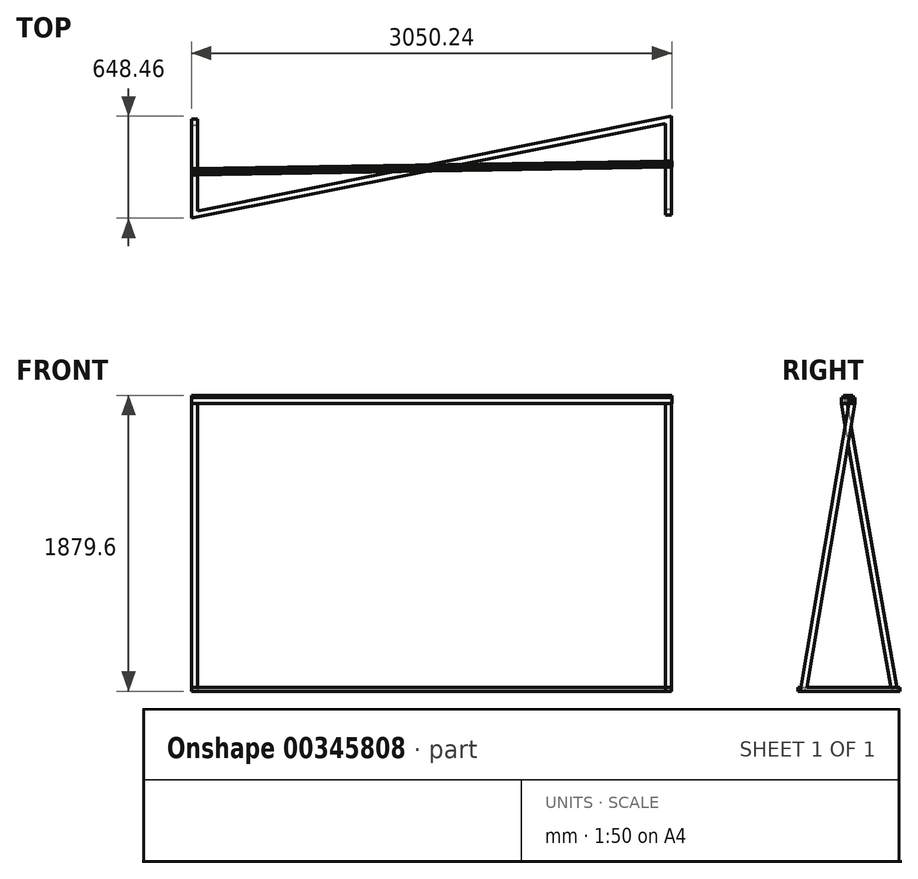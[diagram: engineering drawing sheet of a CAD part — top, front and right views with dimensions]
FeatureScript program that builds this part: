
annotation { "Feature Type Name" : "Feature", "Feature Type Description" : "" }
export const myFeature = defineFeature(function(context is Context, id is Id, definition is map)
    precondition{}
    {
        {
            var Q0;
            Q0=qCreatedBy(makeId("Top.planeOp"),FACE);
            var sketch = newSketch(context, id + "F0", { "sketchPlane" : qUnion([Q0])});
            skLineSegment(sketch, "E0.left", {"start": v(1524, 324.23) * mm, "end": v(1524, -304.8) * mm});
            skLineSegment(sketch, "E0.right", {"start": v(-1524, 304.8) * mm, "end": v(-1524, -324.23) * mm});
            skPoint(sketch, "E0.middle", {"position": v(0, 0) * mm});
            skLineSegment(sketch, "E1", {"start": v(1524, -304.8) * mm, "end": v(1485.9, -304.8) * mm});
            skLineSegment(sketch, "E2", {"start": v(-1485.9, -277.75) * mm, "end": v(-1485.9, 304.8) * mm});
            skLineSegment(sketch, "E3", {"start": v(1485.9, -304.8) * mm, "end": v(1485.9, 277.75) * mm});
            skLineSegment(sketch, "E4", {"start": v(0, 0) * mm, "end": v(-3.74, 18.68) * mm});
            skLineSegment(sketch, "E5", {"start": v(-1485.9, -277.75) * mm, "end": v(1524, 324.23) * mm});
            skLineSegment(sketch, "E6.MirrorCS", {"start": v(-1524, -324.23) * mm, "end": v(1485.9, 277.75) * mm});
            skLineSegment(sketch, "E7", {"start": v(-1524, 304.8) * mm, "end": v(-1485.9, 304.8) * mm});
            skPoint(sketch, "E8", {"position": v(1524, 9.71) * mm});
            skPoint(sketch, "E9", {"position": v(-1524, -9.71) * mm});
            skLineSegment(sketch, "E10.0", {"start": v(1485.78, 24.87) * mm, "end": v(-1386.42, 6.57) * mm});
            skLineSegment(sketch, "E11.MirrorCS", {"start": v(1486.02, -9.58) * mm, "end": v(-1357.54, -27.7) * mm});
            skLineSegment(sketch, "E12", {"start": v(-1357.54, -27.7) * mm, "end": v(-1307.98, -27.39) * mm});
            skLineSegment(sketch, "E13", {"start": v(-1486.02, 5.93) * mm, "end": v(-1485.9, 183.73) * mm});
            skLineSegment(sketch, "E14", {"start": v(-1307.98, -27.39) * mm, "end": v(-1485.9, 183.73) * mm});
            skLineSegment(sketch, "E15", {"start": v(-1307.98, -27.39) * mm, "end": v(-1396.94, 78.17) * mm});
            skLineSegment(sketch, "E16", {"start": v(-1396.94, 78.17) * mm, "end": v(-1426.08, 53.62) * mm});
            skLineSegment(sketch, "E17", {"start": v(-1426.08, 53.62) * mm, "end": v(-1386.42, 6.57) * mm});
            skLineSegment(sketch, "E18", {"start": v(-1357.54, -27.7) * mm, "end": v(-1386.42, 6.57) * mm});
            skLineSegment(sketch, "E19", {"start": v(-1426.08, 53.62) * mm, "end": v(-1485.96, 124.68) * mm});
            skSolve(sketch);
        }
        {
            var Q0;
            {var subQ9=sQuery(id+"F0.wireOp",EDGE,"E0.left");Q0=makeQuery(id+"F0.imprint","IMPRINT",FACE,{"disambiguationData":[TD([[makeQuery(id+"F0.imprint","IMPRINT",EDGE,{"derivedFrom":subQ9}),-1.0]])]});}
            var Q1;
            {var subQ0=sQuery(id+"F0.wireOp",EDGE,"E13");var subQ3=sQuery(id+"F0.wireOp",EDGE,"E19");var subQ5=makeQuery(id+"F0.imprint","INTERSECT",VERTEX,{"derivedFrom":[subQ0,subQ3]});Q1=makeQuery(id+"F0.imprint","IMPRINT",FACE,{"disambiguationData":[TD([[makeQuery(id+"F0.imprint","IMPRINT",EDGE,{"disambiguationData":[TD([[subQ5,1.0]])],"derivedFrom":subQ3}),-1.0]])]});}
            var Q2;
            {var subQ0=sQuery(id+"F0.wireOp",EDGE,"E10.0");var subQ2=sQuery(id+"F0.wireOp",EDGE,"E5");var subQ3=makeQuery(id+"F0.imprint","INTERSECT",VERTEX,{"derivedFrom":[subQ2,subQ0]});Q2=makeQuery(id+"F0.imprint","IMPRINT",FACE,{"disambiguationData":[TD([[makeQuery(id+"F0.imprint","IMPRINT",EDGE,{"disambiguationData":[TD([[subQ3,1.0]])],"derivedFrom":subQ2}),-1.0]])]});}
            var Q3;
            {var subQ0=sQuery(id+"F0.wireOp",EDGE,"E5");var subQ1=sQuery(id+"F0.wireOp",EDGE,"E4");var subQ2=makeQuery(id+"F0.imprint","INTERSECT",VERTEX,{"derivedFrom":[subQ1,subQ0]});Q3=makeQuery(id+"F0.imprint","IMPRINT",FACE,{"disambiguationData":[TD([[makeQuery(id+"F0.imprint","IMPRINT",EDGE,{"disambiguationData":[TD([[subQ2,1.0]])],"derivedFrom":subQ1}),1.0]])]});}
            var Q4;
            {var subQ11=sQuery(id+"F0.wireOp",EDGE,"E0.right");Q4=makeQuery(id+"F0.imprint","IMPRINT",FACE,{"disambiguationData":[TD([[makeQuery(id+"F0.imprint","IMPRINT",EDGE,{"derivedFrom":subQ11}),1.0]])]});}
            extrude(context, id + "F1", {"entities" : qUnion([Q0, Q1, Q2, Q3, Q4]), "depth" : 25.4 * mm});
        }
        {
            var Q0;
            Q0=makeQuery(id+"F1.opExtrude","SWEPT_FACE",FACE,{"disambiguationData":[OSD([sQuery(id+"F0.wireOp",EDGE,"E0.left")])]});
            var sketch = newSketch(context, id + "F2", { "sketchPlane" : qUnion([Q0])});
            skLineSegment(sketch, "E20", {"start": v(0, 0) * mm, "end": v(0, 1828.8) * mm});
            skLineSegment(sketch, "E21", {"start": v(0, 1828.8) * mm, "end": v(-304.8, 25.4) * mm});
            skLineSegment(sketch, "E22", {"start": v(0, 1828.8) * mm, "end": v(37.57, 1822.45) * mm});
            skLineSegment(sketch, "E23", {"start": v(38.64, 1828.8) * mm, "end": v(-266.16, 25.4) * mm});
            skLineSegment(sketch, "E24", {"start": v(38.64, 1828.8) * mm, "end": v(0, 1828.8) * mm});
            skLineSegment(sketch, "E25", {"start": v(-266.16, 25.4) * mm, "end": v(-304.8, 25.4) * mm});
            skSolve(sketch);
        }
        {
            var Q0;
            Q0 = qSketchRegion(id + "F2", true);
            var Q1;
            {var subQ0=sQuery(id+"F2.wireOp",EDGE,"E21");Q1=makeQuery(id+"F2.imprint","IMPRINT",FACE,{"disambiguationData":[TD([[makeQuery(id+"F2.imprint","IMPRINT",EDGE,{"derivedFrom":subQ0}),1.0]])]});}
            extrude(context, id + "F3", {"entities" : qUnion([Q0, Q1]), "operationType" : NewBodyOperationType.ADD, "oppositeDirection" : true, "depth" : 38.1 * mm});
        }
        {
            var Q0;
            Q0=makeQuery(id+"F1.opExtrude","SWEPT_FACE",FACE,{"disambiguationData":[OSD([sQuery(id+"F0.wireOp",EDGE,"E0.right")])]});
            var sketch = newSketch(context, id + "F4", { "sketchPlane" : qUnion([Q0])});
            skLineSegment(sketch, "E26", {"start": v(9.71, 0) * mm, "end": v(9.71, 1828.8) * mm});
            skPoint(sketch, "E26.endSnap0", {"position": v(9.71, 25.4) * mm});
            skLineSegment(sketch, "E27", {"start": v(9.71, 1828.8) * mm, "end": v(-304.8, 25.4) * mm});
            skLineSegment(sketch, "E28", {"start": v(9.71, 1828.8) * mm, "end": v(47.25, 1822.25) * mm});
            skLineSegment(sketch, "E29", {"start": v(48.39, 1828.8) * mm, "end": v(-266.12, 25.4) * mm});
            skLineSegment(sketch, "E30", {"start": v(9.71, 1828.8) * mm, "end": v(49.22, 1828.8) * mm});
            skSolve(sketch);
        }
        {
            var Q0;
            Q0 = qSketchRegion(id + "F4", true);
            var Q1;
            {var subQ0=sQuery(id+"F4.wireOp",EDGE,"E27");Q1=makeQuery(id+"F4.imprint","IMPRINT",FACE,{"disambiguationData":[TD([[makeQuery(id+"F4.imprint","IMPRINT",EDGE,{"derivedFrom":subQ0}),1.0]])]});}
            extrude(context, id + "F5", {"entities" : qUnion([Q0, Q1]), "operationType" : NewBodyOperationType.ADD, "oppositeDirection" : true, "depth" : 38.1 * mm});
        }
        {
            var Q0;
            Q0=makeQuery(id+"F5.opExtrude","SWEPT_FACE",FACE,{"disambiguationData":[OSD([sQuery(id+"F4.wireOp",EDGE,"E30")])]});
            var sketch = newSketch(context, id + "F6", { "sketchPlane" : qUnion([Q0])});
            skLineSegment(sketch, "E31", {"start": v(-1524, -48.39) * mm, "end": v(1526.04, 0) * mm});
            skLineSegment(sketch, "E32", {"start": v(-1524, -9.71) * mm, "end": v(1526.04, 38.68) * mm});
            skLineSegment(sketch, "E33", {"start": v(-1524, -48.39) * mm, "end": v(-1524, -9.71) * mm});
            skLineSegment(sketch, "E34", {"start": v(1526.04, 0) * mm, "end": v(1526.04, 38.68) * mm});
            skLineSegment(sketch, "E35.0", {"start": v(-1523.9, -35.4) * mm, "end": v(1526.14, 12.99) * mm});
            skLineSegment(sketch, "E36.0", {"start": v(-1524.1, -22.7) * mm, "end": v(1525.94, 25.69) * mm});
            skLineSegment(sketch, "E37", {"start": v(-1523.9, -35.4) * mm, "end": v(-1524.1, -22.7) * mm});
            skLineSegment(sketch, "E38", {"start": v(1526.14, 12.99) * mm, "end": v(1525.94, 25.69) * mm});
            skSolve(sketch);
        }
        {
            var Q0;
            Q0 = qSketchRegion(id + "F6", true);
            extrude(context, id + "F7", {"entities" : qUnion([Q0]), "operationType" : NewBodyOperationType.ADD, "depth" : 38.1 * mm});
        }
        {
            var Q0;
            Q0=makeQuery(id+"F7.opExtrude","CAP_FACE",FACE,{"disambiguationData":[OSD([sQuery(id+"F6.wireOp",EDGE,"E31"),sQuery(id+"F6.wireOp",EDGE,"E32"),sQuery(id+"F6.wireOp",EDGE,"E33"),sQuery(id+"F6.wireOp",EDGE,"E34"),sQuery(id+"F6.wireOp",EDGE,"E35.0"),sQuery(id+"F6.wireOp",EDGE,"E36.0"),sQuery(id+"F6.wireOp",EDGE,"E37"),sQuery(id+"F6.wireOp",EDGE,"E38")])],"isStart":false});
            var sketch = newSketch(context, id + "F8", { "sketchPlane" : qUnion([Q0])});
            skLineSegment(sketch, "E39.0", {"start": v(1525.94, 25.69) * mm, "end": v(-1524.1, -22.7) * mm});
            skLineSegment(sketch, "E40.0", {"start": v(1526.14, 12.99) * mm, "end": v(-1523.9, -35.4) * mm});
            skLineSegment(sketch, "E41", {"start": v(1526.04, 12.99) * mm, "end": v(1525.94, 25.69) * mm});
            skLineSegment(sketch, "E42", {"start": v(-1524.1, -22.7) * mm, "end": v(-1523.9, -35.4) * mm});
            skSolve(sketch);
        }
        {
            var Q0;
            Q0 = qSketchRegion(id + "F8", true);
            extrude(context, id + "F9", {"entities" : qUnion([Q0]), "operationType" : NewBodyOperationType.ADD, "depth" : 12.7 * mm});
        }
    });
